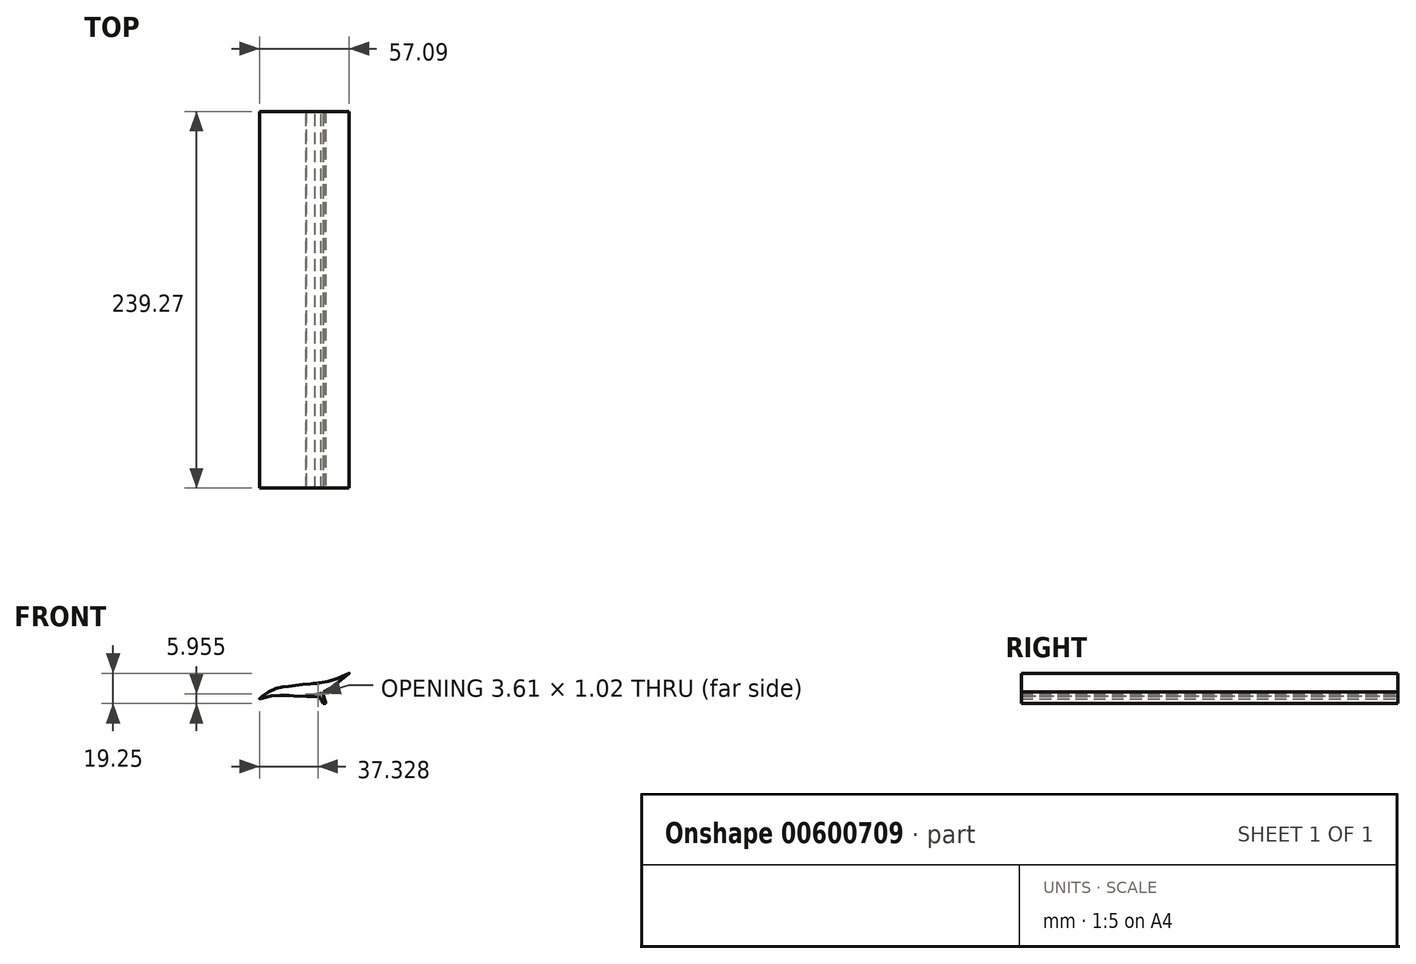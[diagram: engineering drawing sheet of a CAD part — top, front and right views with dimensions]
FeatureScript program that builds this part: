
annotation { "Feature Type Name" : "Feature", "Feature Type Description" : "" }
export const myFeature = defineFeature(function(context is Context, id is Id, definition is map)
    precondition{}
    {
        {
            var Q0;
            Q0=qCreatedBy(makeId("Front.planeOp"),FACE);
            var sketch = newSketch(context, id + "F0", { "sketchPlane" : qUnion([Q0])});
            skFitSpline(sketch, "E0", {"points": [v(0, 0) * mm, v(-12.9, -9.86) * mm, v(-20.34, -13.47) * mm, v(-32.29, -14.6) * mm, v(-50.32, -14.37) * mm, v(-57.09, -16.18) * mm, v(-48.52, -10.31) * mm, v(-38.82, -8.28) * mm, v(-26.87, -6.93) * mm, v(-9.29, -4) * mm, v(0, 0) * mm]});
            skSolve(sketch);
        }
        {
            var Q0;
            Q0=makeQuery(id+"F0.imprint","IMPRINT",FACE,{"disambiguationData":[TD([[makeQuery(id+"F0.imprint","IMPRINT",EDGE,{"derivedFrom":sQuery(id+"F0.wireOp",EDGE,"E0")}),-1.0]])]});
            extrude(context, id + "F1", {"entities" : qUnion([Q0]), "depth" : 127 * mm, "offsetDistance" : 25.4 * mm});
        }
        {
            var Q0;
            Q0=makeQuery(id+"F1.opExtrude","CAP_FACE",FACE,{"disambiguationData":[OSD([sQuery(id+"F0.wireOp",EDGE,"E0")])],"isStart":false});
            extrude(context, id + "F2", {"entities" : qUnion([Q0]), "operationType" : NewBodyOperationType.ADD, "depth" : 112.27 * mm, "offsetDistance" : 25.4 * mm});
        }
        {
            var Q0;
            Q0=qCreatedBy(makeId("Front.planeOp"),FACE);
            var sketch = newSketch(context, id + "F3", { "sketchPlane" : qUnion([Q0])});
            skFitSpline(sketch, "E1", {"points": [v(-16.12, -11.94) * mm, v(-18.1, -12.8) * mm, v(-21.57, -13.75) * mm, v(-27.5, -14.55) * mm, v(-22.99, -14.55) * mm, v(-20.9, -14.55) * mm, v(-19.24, -14.74) * mm, v(-18.4, -15.69) * mm, v(-17.77, -16.83) * mm, v(-16.97, -18.25) * mm, v(-16.45, -19.1) * mm, v(-15.78, -19.15) * mm, v(-14.98, -19.1) * mm, v(-15.36, -17.44) * mm, v(-16.02, -15.26) * mm, v(-16.5, -12.94) * mm, v(-16.12, -11.94) * mm]});
            skSolve(sketch);
        }
        {
            var Q0;
            Q0=makeQuery(id+"F3.imprint","IMPRINT",FACE,{"disambiguationData":[TD([[makeQuery(id+"F3.imprint","IMPRINT",EDGE,{"derivedFrom":sQuery(id+"F3.wireOp",EDGE,"E1")}),1.0]])]});
            extrude(context, id + "F4", {"entities" : qUnion([Q0]), "operationType" : NewBodyOperationType.ADD, "depth" : 127 * mm, "offsetDistance" : 25.4 * mm});
        }
        {
            var Q0;
            Q0=makeQuery(id+"F4.opExtrude","CAP_FACE",FACE,{"disambiguationData":[OSD([sQuery(id+"F3.wireOp",EDGE,"E1")])],"isStart":false});
            extrude(context, id + "F5", {"entities" : qUnion([Q0]), "operationType" : NewBodyOperationType.ADD, "depth" : 112.27 * mm, "offsetDistance" : 25.4 * mm});
        }
    });
